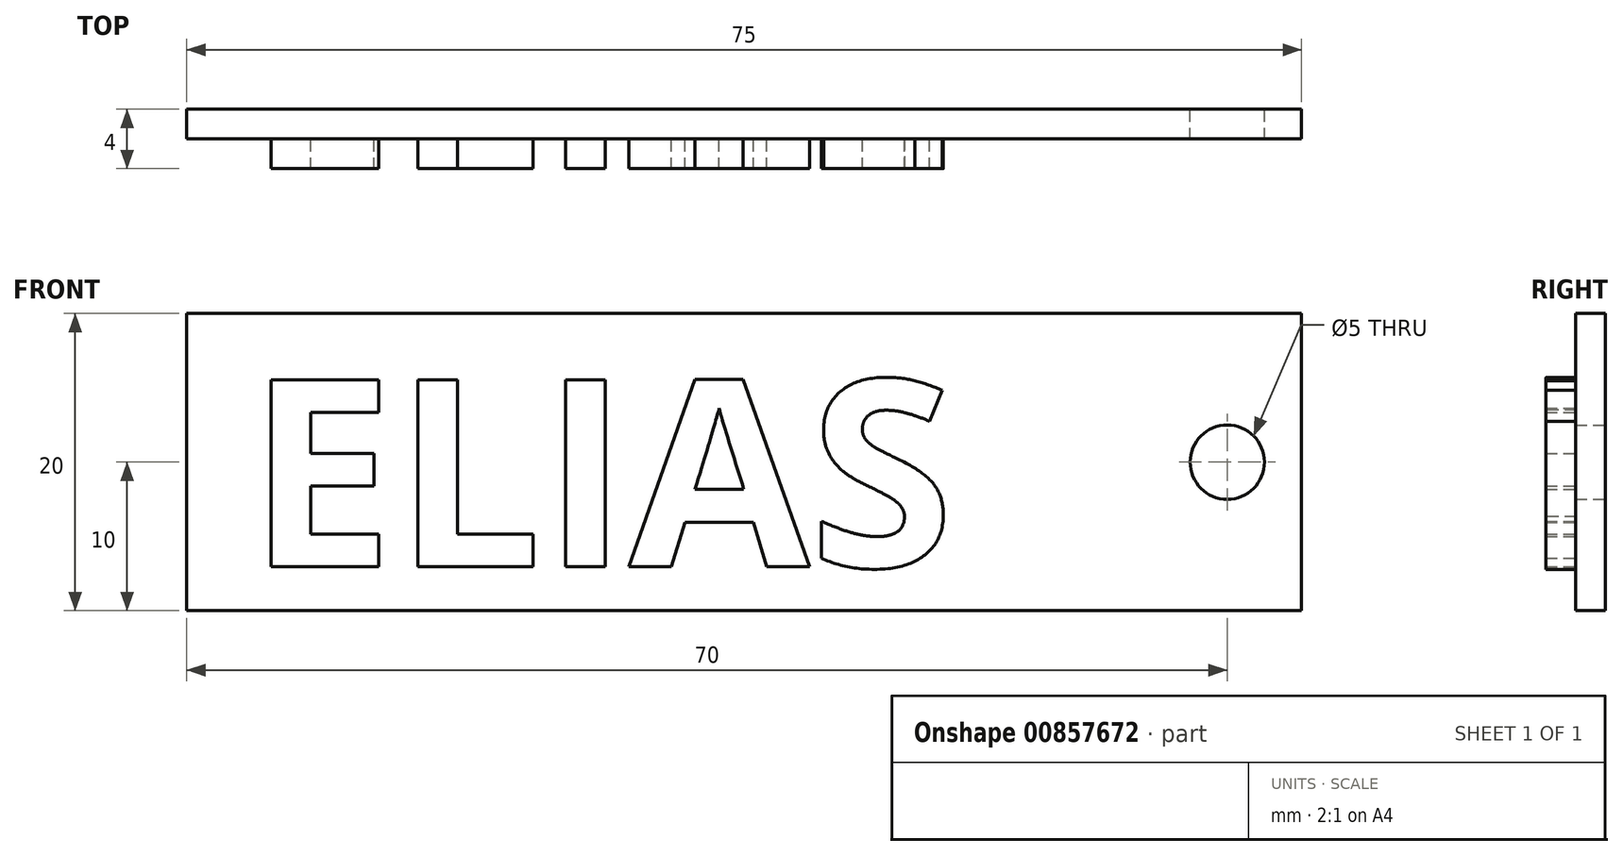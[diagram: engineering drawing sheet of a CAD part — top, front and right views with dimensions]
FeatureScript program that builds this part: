
annotation { "Feature Type Name" : "Feature", "Feature Type Description" : "" }
export const myFeature = defineFeature(function(context is Context, id is Id, definition is map)
    precondition{}
    {
        {
            var Q0;
            Q0=qCreatedBy(makeId("Front.planeOp"),FACE);
            var sketch = newSketch(context, id + "F0", { "sketchPlane" : qUnion([Q0])});
            skLineSegment(sketch, "E0.bottom", {"start": v(0, 0) * mm, "end": v(75, 0) * mm});
            skLineSegment(sketch, "E0.top", {"start": v(0, -20) * mm, "end": v(75, -20) * mm});
            skLineSegment(sketch, "E0.left", {"start": v(0, 0) * mm, "end": v(0, -20) * mm});
            skLineSegment(sketch, "E0.right", {"start": v(75, 0) * mm, "end": v(75, -20) * mm});
            skCircle(sketch, "E1", {"center": v(70, -10) * mm, "radius": 2.5 * mm});
            skSolve(sketch);
        }
        {
            var Q0;
            Q0=makeQuery(id+"F0.imprint","IMPRINT",FACE,{"disambiguationData":[TD([[makeQuery(id+"F0.imprint","IMPRINT",EDGE,{"derivedFrom":sQuery(id+"F0.wireOp",EDGE,"E0.bottom")}),-1.0]])]});
            var sketch = newSketch(context, id + "F1", { "sketchPlane" : qUnion([Q0])});
            skText(sketch, "E2", { "text": "ELIAS", "fontName": "OpenSans-Bold.ttf"});
            const initialGuessF1  = {"E2": [0.00687, -0.0144, 1, 0, 0.00872]};
            skSetInitialGuess(sketch, initialGuessF1);
            skSolve(sketch);
        }
        {
            var Q0;
            Q0=makeQuery(id+"F0.imprint","IMPRINT",FACE,{"disambiguationData":[TD([[makeQuery(id+"F0.imprint","IMPRINT",EDGE,{"derivedFrom":sQuery(id+"F0.wireOp",EDGE,"E0.bottom")}),-1.0]])]});
            var Q1;
            Q1 = qSketchRegion(id + "F0", true);
            extrude(context, id + "F2", {"entities" : qUnion([Q0, Q1]), "depth" : 2 * mm, "offsetDistance" : 25 * mm});
        }
        {
            var Q0;
            Q0 = qSketchRegion(id + "F1", true);
            extrude(context, id + "F3", {"entities" : qUnion([Q0]), "operationType" : NewBodyOperationType.ADD, "depth" : 2 * mm, "offsetDistance" : 25 * mm});
        }
        {
            var Q0;
            Q0=makeQuery(id+"F2.opExtrude","CAP_FACE",FACE,{"disambiguationData":[OSD([sQuery(id+"F0.wireOp",EDGE,"E0.bottom"),sQuery(id+"F0.wireOp",EDGE,"E0.top"),sQuery(id+"F0.wireOp",EDGE,"E0.left"),sQuery(id+"F0.wireOp",EDGE,"E0.right"),sQuery(id+"F0.wireOp",EDGE,"E1")])],"isStart":false});
            var sketch = newSketch(context, id + "F4", { "sketchPlane" : qUnion([Q0])});
            skText(sketch, "E3", { "text": "ELIAS", "fontName": "OpenSans-Bold.ttf"});
            const initialGuessF4  = {"E3": [0.0041, -0.01704, 1, 0, 0.01268]};
            skSetInitialGuess(sketch, initialGuessF4);
            skSolve(sketch);
        }
        {
            var Q0;
            Q0 = qSketchRegion(id + "F4", true);
            extrude(context, id + "F5", {"entities" : qUnion([Q0]), "operationType" : NewBodyOperationType.ADD, "depth" : 2 * mm, "offsetDistance" : 25 * mm});
        }
    });
